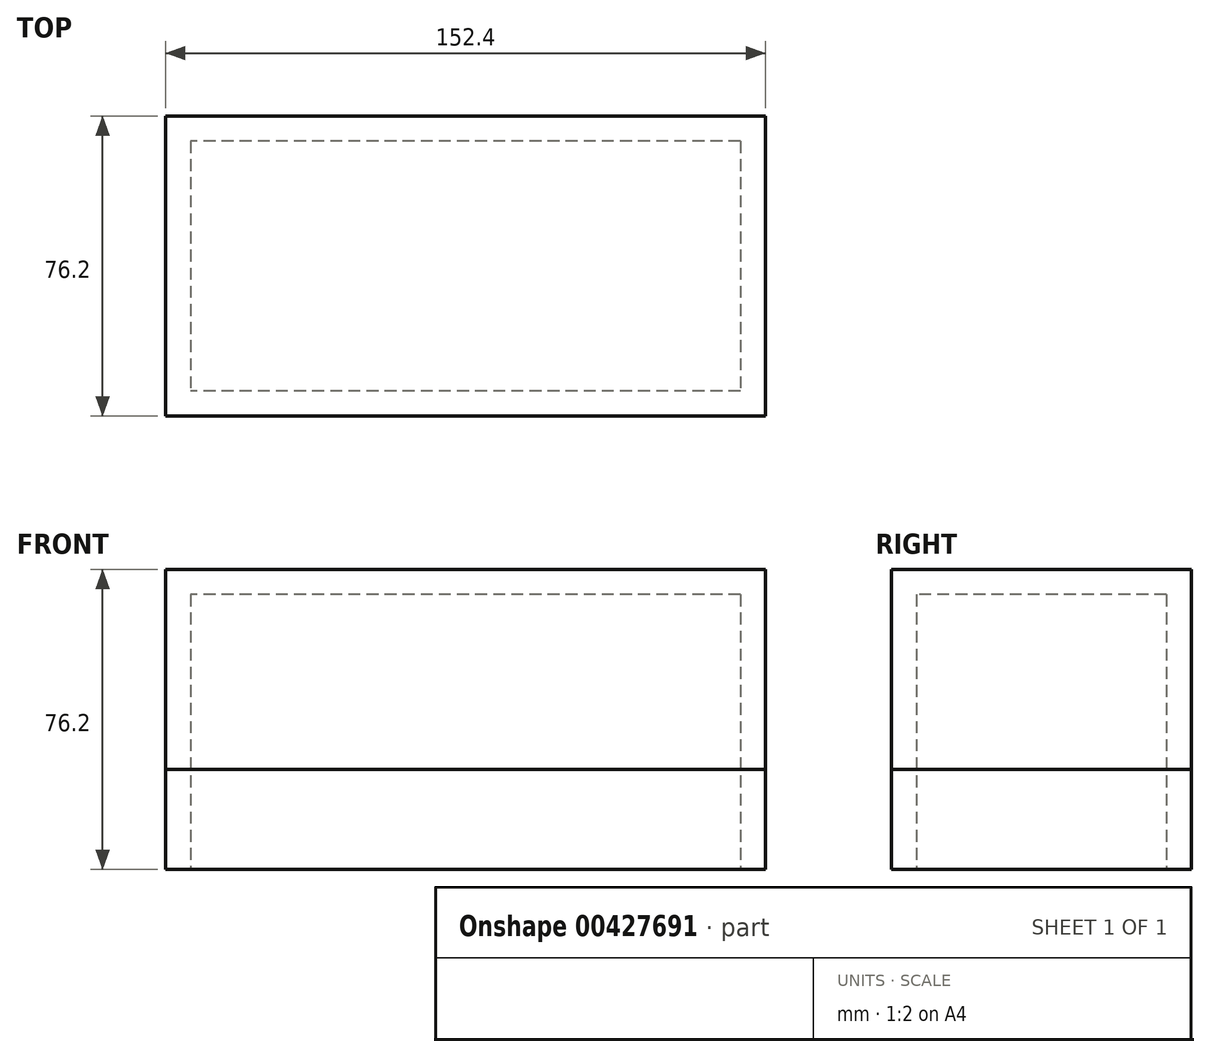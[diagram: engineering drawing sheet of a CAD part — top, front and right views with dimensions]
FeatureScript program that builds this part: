
annotation { "Feature Type Name" : "Feature", "Feature Type Description" : "" }
export const myFeature = defineFeature(function(context is Context, id is Id, definition is map)
    precondition{}
    {
        {
            var Q0;
            Q0=qCreatedBy(makeId("Top.planeOp"),FACE);
            var sketch = newSketch(context, id + "F0", { "sketchPlane" : qUnion([Q0])});
            skLineSegment(sketch, "E0.bottom", {"start": v(76.2, 38.1) * mm, "end": v(-76.2, 38.1) * mm});
            skLineSegment(sketch, "E0.top", {"start": v(76.2, -38.1) * mm, "end": v(-76.2, -38.1) * mm});
            skLineSegment(sketch, "E0.left", {"start": v(76.2, 38.1) * mm, "end": v(76.2, -38.1) * mm});
            skLineSegment(sketch, "E0.right", {"start": v(-76.2, 38.1) * mm, "end": v(-76.2, -38.1) * mm});
            skPoint(sketch, "E0.middle", {"position": v(0, 0) * mm});
            skSolve(sketch);
        }
        {
            var Q0;
            Q0 = qSketchRegion(id + "F0", true);
            extrude(context, id + "F1", {"entities" : qUnion([Q0]), "depth" : 76.2 * mm});
        }
        {
            var Q0;
            Q0=makeQuery(id+"F1.opExtrude","CAP_FACE",FACE,{"disambiguationData":[OSD([sQuery(id+"F0.wireOp",EDGE,"E0.bottom"),sQuery(id+"F0.wireOp",EDGE,"E0.top"),sQuery(id+"F0.wireOp",EDGE,"E0.left"),sQuery(id+"F0.wireOp",EDGE,"E0.right")])],"isStart":true});
            shell(context, id + "F2", {"entities" : qUnion([Q0]), "thickness" : 6.35 * mm});
        }
        {
            var Q0;
            Q0=qCreatedBy(makeId("Top.planeOp"),FACE);
            var sketch = newSketch(context, id + "F3", { "sketchPlane" : qUnion([Q0])});
            skLineSegment(sketch, "E1.bottom", {"start": v(76.2, 38.1) * mm, "end": v(-76.2, 38.1) * mm});
            skLineSegment(sketch, "E1.top", {"start": v(76.2, -38.1) * mm, "end": v(-76.2, -38.1) * mm});
            skLineSegment(sketch, "E1.left", {"start": v(76.2, 38.1) * mm, "end": v(76.2, -38.1) * mm});
            skLineSegment(sketch, "E1.right", {"start": v(-76.2, 38.1) * mm, "end": v(-76.2, -38.1) * mm});
            skPoint(sketch, "E1.middle", {"position": v(0, 0) * mm});
            skSolve(sketch);
        }
        {
            var Q0;
            Q0 = qSketchRegion(id + "F3", true);
            extrude(context, id + "F4", {"entities" : qUnion([Q0]), "depth" : 25.4 * mm});
        }
    });
